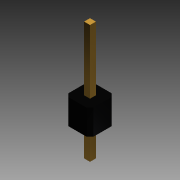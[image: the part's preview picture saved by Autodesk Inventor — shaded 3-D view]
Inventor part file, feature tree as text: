
AUTODESK INVENTOR PART (.ipt)
format: ipt  version: 2013 SP1 (Build 170176100, 176)  size: 102,400 bytes
history: native  units: mm
features: extrude x2, sketch x2, chamfer x1
ambient origin geometry x8: Origin, YZ Plane, XZ Plane, XY Plane, X Axis, Y Axis, Z Axis, Center Point
bodies: Volumenkörper1 (feature_tree), Volumenkörper2 (feature_tree)
feature tree (5):
  extrude  "Extrusion1"  Depth=2.54mm
  chamfer  "Fase1"  Distance=2.54mm
  extrude  "Extrusion2"  Depth=0.6mm
  sketch  "Skizze1"  dims[d0=2.54mm d1=2.54mm d2=2.54mm d3=0.0mm]
  sketch  "Skizze2"  dims[d4=0.35mm d5=2.0mm d6=45.0deg d7=0.6mm d8=0.6mm d9=9.0mm d10=3.0mm d11=0.0mm d12=0.0mm]
